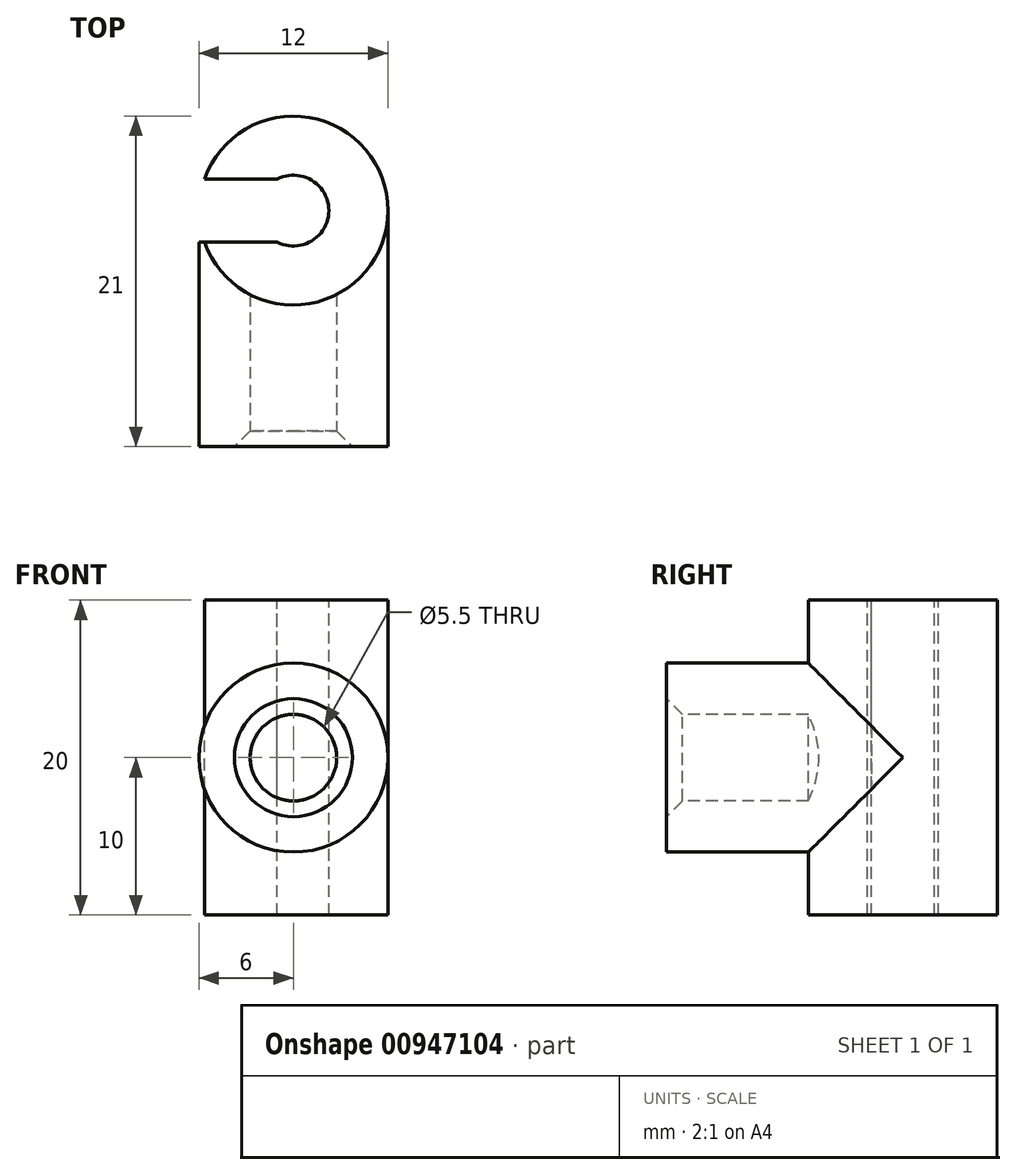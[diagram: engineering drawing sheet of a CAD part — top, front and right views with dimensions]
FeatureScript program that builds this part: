
annotation { "Feature Type Name" : "Feature", "Feature Type Description" : "" }
export const myFeature = defineFeature(function(context is Context, id is Id, definition is map)
    precondition{}
    {
        {
            var Q0;
            Q0=qCreatedBy(makeId("Top.planeOp"),FACE);
            var sketch = newSketch(context, id + "F0", { "sketchPlane" : qUnion([Q0])});
            skCircle(sketch, "E0", {"center": v(0, 0) * mm, "radius": 6 * mm});
            skSolve(sketch);
        }
        {
            var Q0;
            Q0=makeQuery(id+"F0.imprint","IMPRINT",FACE,{"disambiguationData":[TD([[makeQuery(id+"F0.imprint","IMPRINT",EDGE,{"derivedFrom":sQuery(id+"F0.wireOp",EDGE,"E0")}),1.0]])]});
            extrude(context, id + "F1", {"entities" : qUnion([Q0]), "oppositeDirection" : true, "depth" : 20 * mm, "offsetDistance" : 25 * mm});
        }
        {
            var Q0;
            Q0=makeQuery(id+"F1.opExtrude","CAP_FACE",FACE,{"disambiguationData":[OSD([sQuery(id+"F0.wireOp",EDGE,"E0")])],"isStart":true});
            var sketch = newSketch(context, id + "F2", { "sketchPlane" : qUnion([Q0])});
            skCircle(sketch, "E1", {"center": v(0, 0) * mm, "radius": 2.25 * mm});
            skSolve(sketch);
        }
        {
            var Q0;
            Q0=qCreatedBy(makeId("Front.planeOp"),FACE);
            cPlane(context, id + "F3", {"entities" : qUnion([Q0]), "cplaneType" : CPlaneType.OFFSET, "offset" : 15 * mm, "width" : 150 * mm, "height" : 150 * mm});
        }
        {
            var Q0;
            Q0=qCreatedBy(id+"F3.planeOp",FACE);
            var sketch = newSketch(context, id + "F4", { "sketchPlane" : qUnion([Q0])});
            skCircle(sketch, "E2", {"center": v(0, -10) * mm, "radius": 6 * mm});
            skCircle(sketch, "E3", {"center": v(0, -10) * mm, "radius": 2.75 * mm});
            skSolve(sketch);
        }
        {
            var Q0;
            Q0=makeQuery(id+"F4.imprint","IMPRINT",FACE,{"disambiguationData":[TD([[makeQuery(id+"F4.imprint","IMPRINT",EDGE,{"derivedFrom":sQuery(id+"F4.wireOp",EDGE,"E2")}),1.0]])]});
            extrude(context, id + "F5", {"entities" : qUnion([Q0]), "operationType" : NewBodyOperationType.ADD, "oppositeDirection" : true, "depth" : 15 * mm, "offsetDistance" : 25 * mm});
        }
        {
            var Q0;
            Q0=makeQuery(id+"F2.imprint","IMPRINT",FACE,{"disambiguationData":[TD([[makeQuery(id+"F2.imprint","IMPRINT",EDGE,{"derivedFrom":sQuery(id+"F2.wireOp",EDGE,"E1")}),1.0]])]});
            extrude(context, id + "F6", {"entities" : qUnion([Q0]), "operationType" : NewBodyOperationType.REMOVE, "endBound" : BoundingType.UP_TO_NEXT, "oppositeDirection" : true, "depth" : 25 * mm, "offsetDistance" : 25 * mm});
        }
        {
            var Q0;
            Q0=makeQuery(id+"F1.opExtrude","CAP_FACE",FACE,{"disambiguationData":[OSD([sQuery(id+"F0.wireOp",EDGE,"E0")])],"isStart":true});
            var sketch = newSketch(context, id + "F7", { "sketchPlane" : qUnion([Q0])});
            skLineSegment(sketch, "E4.bottom", {"start": v(-8.53, 2) * mm, "end": v(0, 2) * mm});
            skLineSegment(sketch, "E4.top", {"start": v(-8.53, -2) * mm, "end": v(0, -2) * mm});
            skLineSegment(sketch, "E4.left", {"start": v(-8.53, 2) * mm, "end": v(-8.53, -2) * mm});
            skPoint(sketch, "E4.middle", {"position": v(0, 0) * mm});
            skLineSegment(sketch, "E5", {"start": v(0, 2) * mm, "end": v(0, -2) * mm});
            skSolve(sketch);
        }
        {
            var Q0;
            {var subQ0=sQuery(id+"F7.wireOp",EDGE,"E4.bottom");var subQ1=makeQuery(id+"F1.opExtrude","CAP_EDGE",EDGE,{"disambiguationData":[OSD([sQuery(id+"F0.wireOp",EDGE,"E0")])],"isStart":true});var subQ2=makeQuery(id+"F7.imprint","INTERSECT",VERTEX,{"derivedFrom":[subQ1,subQ0]});Q0=makeQuery(id+"F7.imprint","IMPRINT",FACE,{"disambiguationData":[TD([[makeQuery(id+"F7.imprint","IMPRINT",EDGE,{"disambiguationData":[TD([[subQ2,-1.0]])],"derivedFrom":subQ0}),-1.0]])]});}
            var Q1;
            {var subQ0=sQuery(id+"F7.wireOp",EDGE,"E5");Q1=makeQuery(id+"F7.imprint","IMPRINT",FACE,{"disambiguationData":[TD([[makeQuery(id+"F7.imprint","IMPRINT",EDGE,{"derivedFrom":subQ0}),-1.0]])]});}
            var Q2;
            {var subQ0=sQuery(id+"F7.wireOp",EDGE,"E4.left");Q2=makeQuery(id+"F7.imprint","IMPRINT",FACE,{"disambiguationData":[TD([[makeQuery(id+"F7.imprint","IMPRINT",EDGE,{"derivedFrom":subQ0}),1.0]])]});}
            extrude(context, id + "F8", {"entities" : qUnion([Q0, Q1, Q2]), "operationType" : NewBodyOperationType.REMOVE, "endBound" : BoundingType.UP_TO_NEXT, "oppositeDirection" : true, "depth" : 25 * mm, "offsetDistance" : 25 * mm});
        }
        {
            var Q0;
            Q0=makeQuery(id+"F5.opExtrude","CAP_EDGE",EDGE,{"disambiguationData":[OSD([sQuery(id+"F4.wireOp",EDGE,"E3")])],"isStart":true});
            chamfer(context, id + "F9", {"entities" : qUnion([Q0]), "width" : 1 * mm, "tangentPropagation" : true});
        }
    });
